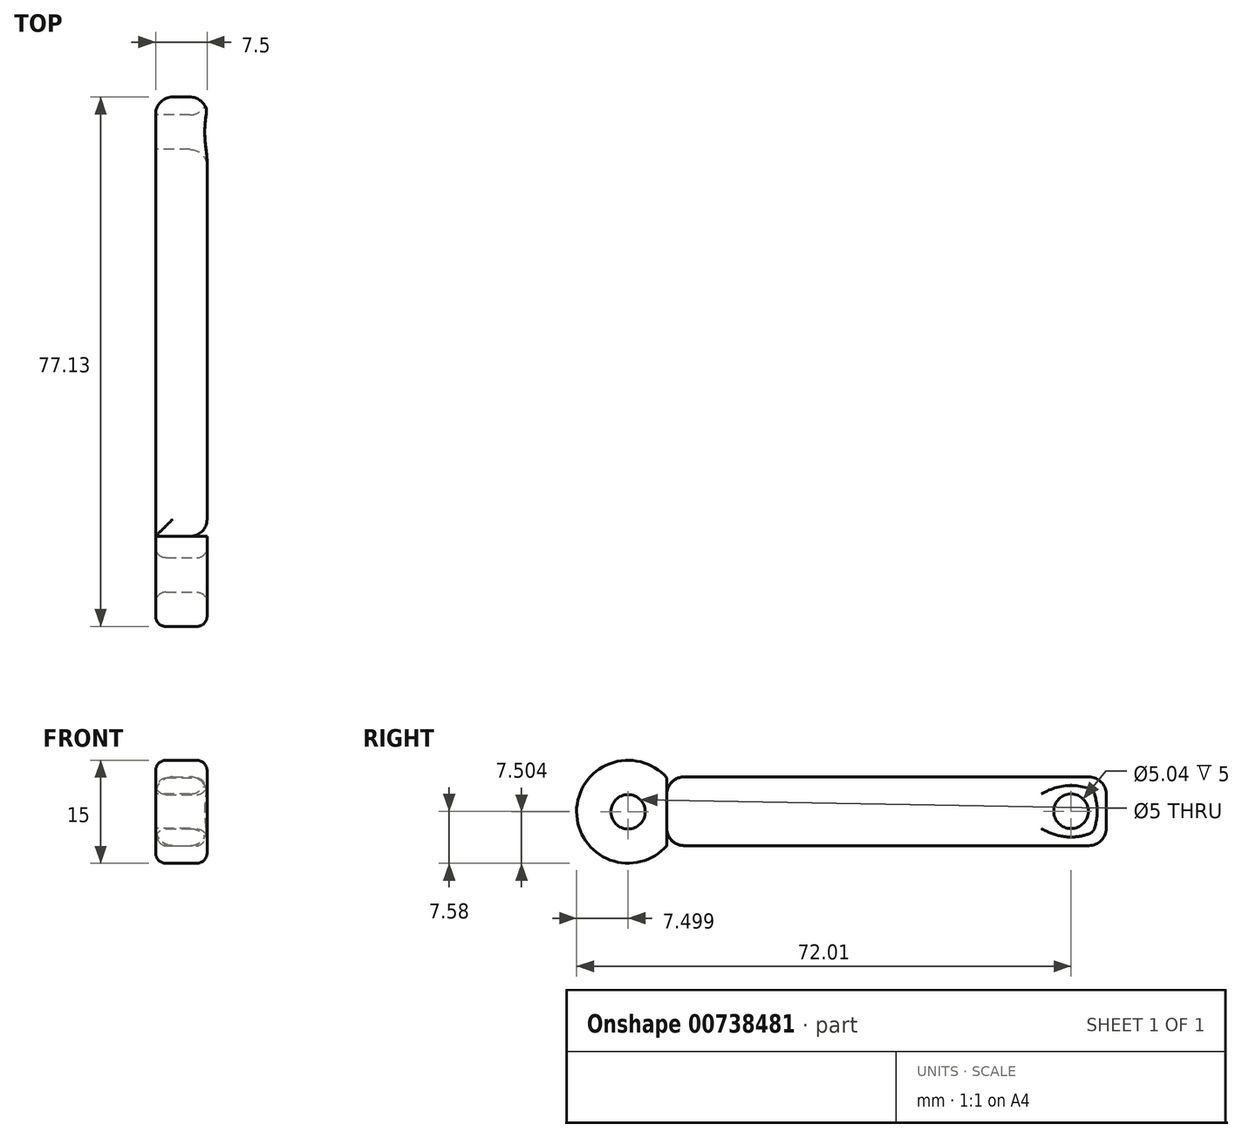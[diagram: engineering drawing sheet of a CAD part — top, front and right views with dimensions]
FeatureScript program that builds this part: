
annotation { "Feature Type Name" : "Feature", "Feature Type Description" : "" }
export const myFeature = defineFeature(function(context is Context, id is Id, definition is map)
    precondition{}
    {
        {
            var Q0;
            Q0=qCreatedBy(makeId("Top.planeOp"),FACE);
            var sketch = newSketch(context, id + "F0", { "sketchPlane" : qUnion([Q0])});
            skLineSegment(sketch, "E0.bottom", {"start": v(-26.52, 45.08) * mm, "end": v(-16.52, 45.08) * mm});
            skLineSegment(sketch, "E0.top", {"start": v(-26.52, -18.92) * mm, "end": v(-16.52, -18.92) * mm});
            skLineSegment(sketch, "E0.left", {"start": v(-26.52, 45.08) * mm, "end": v(-26.52, -18.92) * mm});
            skLineSegment(sketch, "E0.right", {"start": v(-16.52, 45.08) * mm, "end": v(-16.52, -18.92) * mm});
            skSolve(sketch);
        }
        {
            var Q0;
            Q0=makeQuery(id+"F0.imprint","IMPRINT",FACE,{"disambiguationData":[TD([[makeQuery(id+"F0.imprint","IMPRINT",EDGE,{"derivedFrom":sQuery(id+"F0.wireOp",EDGE,"E0.bottom")}),-1.0]])]});
            var sketch = newSketch(context, id + "F1", { "sketchPlane" : qUnion([Q0])});
            skCircle(sketch, "E1", {"center": v(-21.44, 50.71) * mm, "radius": 7.5 * mm});
            skCircle(sketch, "E2", {"center": v(-21.44, 50.71) * mm, "radius": 2.5 * mm});
            skSolve(sketch);
        }
        {
            var Q0;
            Q0=makeQuery(id+"F0.imprint","IMPRINT",FACE,{"disambiguationData":[TD([[makeQuery(id+"F0.imprint","IMPRINT",EDGE,{"derivedFrom":sQuery(id+"F0.wireOp",EDGE,"E0.bottom")}),-1.0]])]});
            var Q1;
            Q1=makeQuery(id+"F1.imprint","IMPRINT",FACE,{"disambiguationData":[TD([[makeQuery(id+"F1.imprint","IMPRINT",EDGE,{"derivedFrom":sQuery(id+"F1.wireOp",EDGE,"E2")}),-1.0]])]});
            extrude(context, id + "F2", {"entities" : qUnion([Q0, Q1]), "depth" : 7.5 * mm, "offsetDistance" : 25 * mm});
        }
        {
            var Q0;
            Q0=makeQuery(id+"F2.opExtrude","CAP_FACE",FACE,{"disambiguationData":[OSD([sQuery(id+"F0.wireOp",EDGE,"E0.bottom"),sQuery(id+"F0.wireOp",EDGE,"E0.top"),sQuery(id+"F0.wireOp",EDGE,"E0.left"),sQuery(id+"F0.wireOp",EDGE,"E0.right")])],"isStart":false});
            var sketch = newSketch(context, id + "F3", { "sketchPlane" : qUnion([Q0])});
            skCircle(sketch, "E3", {"center": v(-21.52, -13.8) * mm, "radius": 2.52 * mm});
            skPoint(sketch, "E3.centerSnap0", {"position": v(-21.52, -18.92) * mm});
            skSolve(sketch);
        }
        {
            var Q0;
            Q0=makeQuery(id+"F3.imprint","IMPRINT",FACE,{"disambiguationData":[TD([[makeQuery(id+"F3.imprint","IMPRINT",EDGE,{"derivedFrom":sQuery(id+"F3.wireOp",EDGE,"E3")}),1.0]])]});
            extrude(context, id + "F4", {"entities" : qUnion([Q0]), "operationType" : NewBodyOperationType.REMOVE, "endBound" : BoundingType.THROUGH_ALL, "oppositeDirection" : true, "depth" : 25 * mm, "offsetDistance" : 25 * mm});
        }
        {
            var Q0;
            {var subQ0=sQuery(id+"F0.wireOp",EDGE,"E0.right");Q0=makeQuery(id+"F2.opExtrude","CAP_EDGE",EDGE,{"disambiguationData":[OSD([subQ0]),TDD([makeQuery(id+"F0.imprint","IMPRINT",EDGE,{"derivedFrom":subQ0})])],"isStart":false});}
            var Q1;
            Q1=makeQuery(id+"F2.opExtrude","CAP_EDGE",EDGE,{"disambiguationData":[OSD([sQuery(id+"F0.wireOp",EDGE,"E0.left")])],"isStart":false});
            var Q2;
            Q2=makeQuery(id+"F2.opExtrude","CAP_EDGE",EDGE,{"disambiguationData":[OSD([sQuery(id+"F0.wireOp",EDGE,"E0.top")])],"isStart":false});
            var Q3;
            Q3=makeQuery(id+"F2.opExtrude","SWEPT_FACE",FACE,{"disambiguationData":[OSD([sQuery(id+"F0.wireOp",EDGE,"E0.top")])]});
            var Q4;
            {var subQ0=sQuery(id+"F0.wireOp",EDGE,"E0.right");Q4=makeQuery(id+"F2.opExtrude","SWEPT_FACE",FACE,{"disambiguationData":[OSD([subQ0]),TDD([makeQuery(id+"F0.imprint","IMPRINT",EDGE,{"derivedFrom":subQ0})])]});}
            var Q5;
            Q5=makeQuery(id+"F2.opExtrude","SWEPT_FACE",FACE,{"disambiguationData":[OSD([sQuery(id+"F0.wireOp",EDGE,"E0.left")])]});
            var Q6;
            Q6=makeQuery(id+"F2.opExtrude","CAP_FACE",FACE,{"disambiguationData":[OSD([sQuery(id+"F0.wireOp",EDGE,"E0.bottom"),sQuery(id+"F0.wireOp",EDGE,"E0.top"),sQuery(id+"F0.wireOp",EDGE,"E0.left"),sQuery(id+"F0.wireOp",EDGE,"E0.right")])],"isStart":true});
            fillet(context, id + "F5", {"entities" : qUnion([Q0, Q1, Q2, Q3, Q4, Q5, Q6]), "radius" : 2.5 * mm, "tangentPropagation" : true, "allowEdgeOverflow" : false});
        }
        {
            var Q0;
            Q0=makeQuery(id+"F2.opExtrude","SWEPT_FACE",FACE,{"disambiguationData":[OSD([sQuery(id+"F1.wireOp",EDGE,"E2")])]});
            var Q1;
            Q1=makeQuery(id+"F2.opExtrude","CAP_EDGE",EDGE,{"disambiguationData":[OSD([sQuery(id+"F1.wireOp",EDGE,"E1")])],"isStart":false});
            var Q2;
            Q2=makeQuery(id+"F2.opExtrude","CAP_EDGE",EDGE,{"disambiguationData":[OSD([sQuery(id+"F1.wireOp",EDGE,"E1")])],"isStart":true});
            fillet(context, id + "F6", {"entities" : qUnion([Q0, Q1, Q2]), "radius" : 1.5 * mm, "tangentPropagation" : true, "allowEdgeOverflow" : false});
        }
        {
            var Q0;
            Q0=makeQuery(id+"F2.opExtrude","SWEPT_BODY",BODY,{"disambiguationData":[OSD([sQuery(id+"F0.wireOp",EDGE,"E0.bottom"),sQuery(id+"F0.wireOp",EDGE,"E0.top"),sQuery(id+"F0.wireOp",EDGE,"E0.left"),sQuery(id+"F0.wireOp",EDGE,"E0.right")])]});
            var Q1;
            Q1=makeQuery(id+"F2.opExtrude","SWEPT_BODY",BODY,{"disambiguationData":[OSD([sQuery(id+"F0.wireOp",EDGE,"E0.bottom"),sQuery(id+"F0.wireOp",EDGE,"E0.right"),sQuery(id+"F1.wireOp",EDGE,"E1"),sQuery(id+"F1.wireOp",EDGE,"E2")])]});
            var Q2;
            {var subQ0=sQuery(id+"F0.wireOp",EDGE,"E0.left");Q2=makeQuery(id+"F5.opFillet","BLEND_EDGE",EDGE,{"disambiguationData":[OD(1.0)],"blendedFrom":[makeQuery(id+"F2.opExtrude","CAP_EDGE",EDGE,{"disambiguationData":[OSD([subQ0])],"isStart":false}),makeQuery(id+"F2.opExtrude","CAP_FACE",FACE,{"disambiguationData":[OSD([sQuery(id+"F0.wireOp",EDGE,"E0.bottom"),sQuery(id+"F0.wireOp",EDGE,"E0.top"),subQ0,sQuery(id+"F0.wireOp",EDGE,"E0.right")])],"isStart":false})],"blendedInto":[makeQuery(id+"F2.opExtrude","CAP_FACE",FACE,{"disambiguationData":[OSD([sQuery(id+"F0.wireOp",EDGE,"E0.bottom"),sQuery(id+"F0.wireOp",EDGE,"E0.top"),subQ0,sQuery(id+"F0.wireOp",EDGE,"E0.right")])],"isStart":false})]});}
            transform(context, id + "F7", {"entities" : qUnion([Q0, Q1]), "transformType" : TransformType.ROTATION, "transformAxis" : qUnion([Q2]), "angle" : 90 * degree, "makeCopy" : false});
        }
        {
            var Q0;
            Q0=makeQuery(id+"F2.opExtrude","SWEPT_BODY",BODY,{"disambiguationData":[OSD([sQuery(id+"F0.wireOp",EDGE,"E0.bottom"),sQuery(id+"F0.wireOp",EDGE,"E0.right"),sQuery(id+"F1.wireOp",EDGE,"E1"),sQuery(id+"F1.wireOp",EDGE,"E2")])]});
            var Q1;
            Q1=makeQuery(id+"F2.opExtrude","SWEPT_BODY",BODY,{"disambiguationData":[OSD([sQuery(id+"F0.wireOp",EDGE,"E0.bottom"),sQuery(id+"F0.wireOp",EDGE,"E0.top"),sQuery(id+"F0.wireOp",EDGE,"E0.left"),sQuery(id+"F0.wireOp",EDGE,"E0.right")])]});
            var Q2;
            {var subQ0=sQuery(id+"F0.wireOp",EDGE,"E0.top");Q2=makeQuery(id+"F5.opFillet","BLEND_EDGE",EDGE,{"blendedFrom":[makeQuery(id+"F2.opExtrude","SWEPT_EDGE",EDGE,{"disambiguationData":[OSD([subQ0,sQuery(id+"F0.wireOp",EDGE,"E0.left")])]}),makeQuery(id+"F2.opExtrude","SWEPT_FACE",FACE,{"disambiguationData":[OSD([subQ0])]})],"blendedInto":[makeQuery(id+"F2.opExtrude","SWEPT_FACE",FACE,{"disambiguationData":[OSD([subQ0])]})]});}
            transform(context, id + "F8", {"entities" : qUnion([Q0, Q1]), "transformType" : TransformType.ROTATION, "transformAxis" : qUnion([Q2]), "angle" : 180 * degree, "makeCopy" : false});
        }
    });
